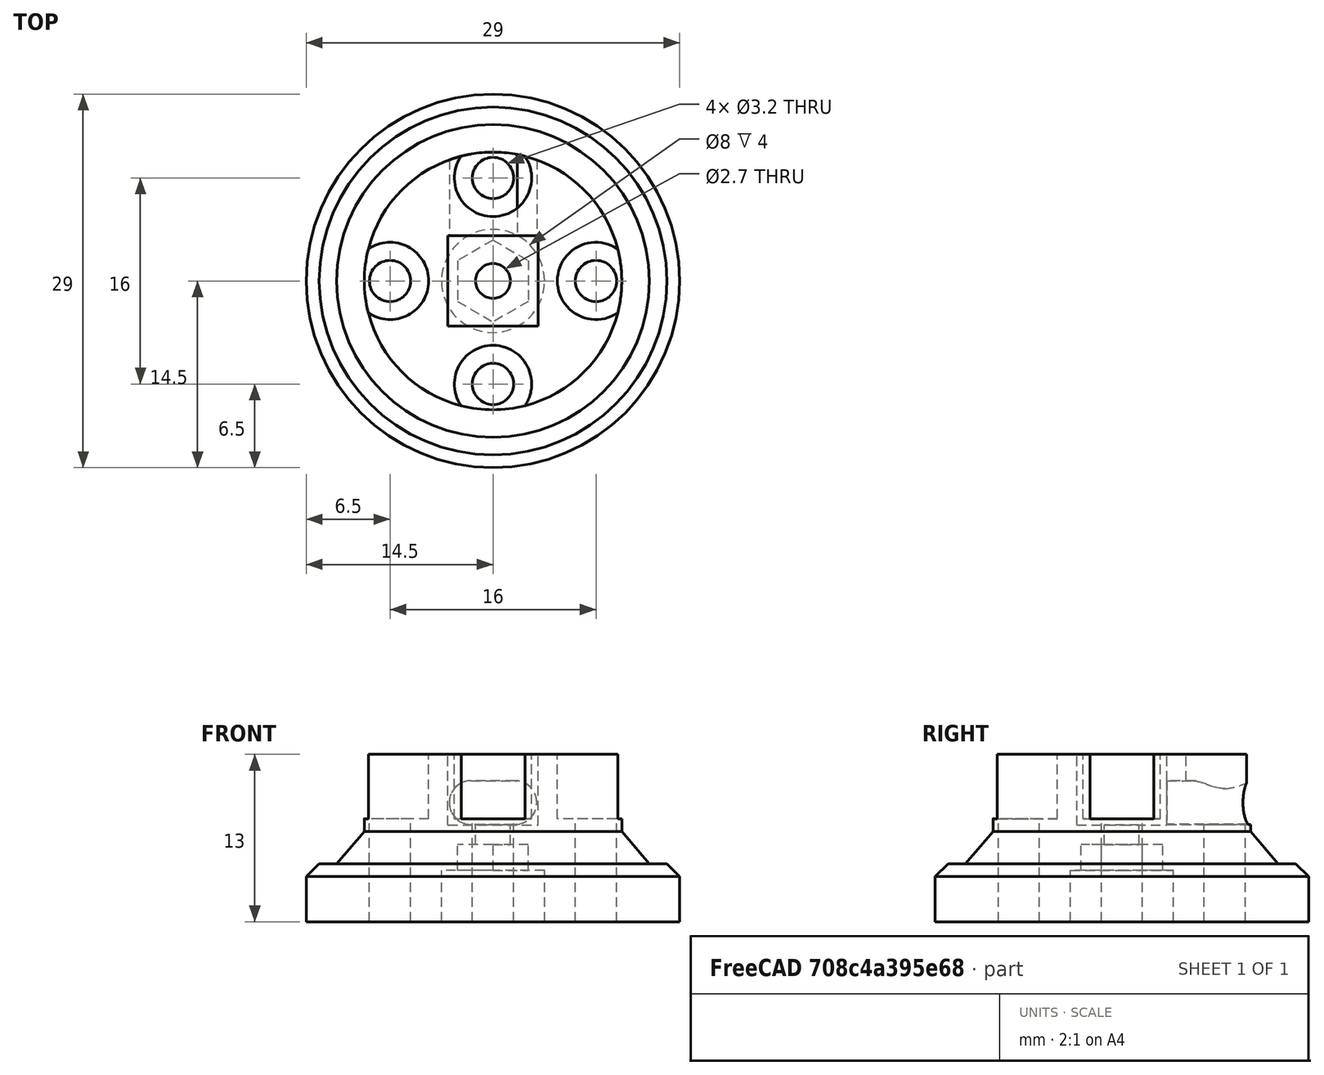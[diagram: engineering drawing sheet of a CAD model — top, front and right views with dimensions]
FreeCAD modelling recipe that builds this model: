
FCSTD DOCUMENT  (FreeCAD 0.15R4671 (Git))
Label: tendon_wheel_ax_fingers
License: CC-BY 3.0
LicenseURL: http://creativecommons.org/licenses/by/3.0/
objects: Part::Cylinder×14, Part::MultiFuse×6, Part::Box×2, Part::Cone×1, Part::Extrusion×1, Part::Mirroring×1, Part::Cut×1, Part::Chamfer×1
note: 27 computed .brp shape members not serialized (recipe doc carries the construction recipe); baked Part::Feature solids carry a one-line shape summary decoded from their .brp

FEATURE [Part::Cylinder] Cylinder
  Angle = 360
  Height = 4.5
  Placement = pos=(0,0,0.5) rot=(0,0,1;0rad)
  Radius = 14.5
FEATURE [Part::Cone] Cone
  Angle = 360
  Height = 3.5
  Placement = pos=(0,0,4) rot=(0,0,1;0rad)
  Radius1 = 13
  Radius2 = 10
FEATURE [Part::Cylinder] Cylinder001
  Angle = 360
  Height = 6.5
  Placement = pos=(0,0,7) rot=(0,0,1;0rad)
  Radius = 10
FEATURE [Part::Cylinder] Cylinder003  label="TopHole003"
  Angle = 360
  Height = 20
  Placement = pos=(-8,0,-7) rot=(0,0,1;0rad)
  Radius = 1.6
FEATURE [Part::Cylinder] Cylinder004  label="TopHole002"
  Angle = 360
  Height = 20
  Placement = pos=(0,-8,-7) rot=(0,0,1;0rad)
  Radius = 1.6
FEATURE [Part::Cylinder] Cylinder005  label="TopHole001"
  Angle = 360
  Height = 20
  Placement = pos=(8,0,-7) rot=(0,0,1;0rad)
  Radius = 1.6
FEATURE [Part::Cylinder] Cylinder006  label="TopHole"
  Angle = 360
  Height = 15
  Placement = pos=(0,8,-7) rot=(0,0,1;0rad)
  Radius = 1.6
FEATURE [Part::Cylinder] Cylinder007  label="TopHole004"
  Angle = 360
  Height = 20
  Placement = pos=(-8,0,3.5) rot=(0,0,1;0rad)
  Radius = 3
FEATURE [Part::Cylinder] Cylinder008  label="TopHole005"
  Angle = 360
  Height = 20
  Placement = pos=(8,0,3.5) rot=(0,0,1;0rad)
  Radius = 3
FEATURE [Part::Cylinder] Cylinder009  label="TopHole006"
  Angle = 360
  Height = 20
  Placement = pos=(0,8,4.5) rot=(0,0,1;0rad)
  Radius = 3
FEATURE [Part::Cylinder] Cylinder010  label="TopHole007"
  Angle = 360
  Height = 20
  Placement = pos=(0,-8,3.5) rot=(0,0,1;0rad)
  Radius = 3
FEATURE [Part::MultiFuse] Fusion001
  Placement = pos=(0,0,5) rot=(0,0,1;0rad)
  Shapes = -> [Cylinder010,Cylinder007,Cylinder005,Cylinder003,Cylinder009,Cylinder004,Cylinder008,Cylinder006]
FEATURE [Part::Cylinder] Cylinder012  label="Cylinder003"
  Angle = 360
  Height = 10
  Placement = pos=(-1.7,12,9.75) rot=(1,0,0;1.5708rad)
  Radius = 1.7
FEATURE [Part::Cylinder] Cylinder013  label="Cylinder004"
  Angle = 360
  Height = 20
  Placement = pos=(0,0,-5) rot=(0,0,1;0rad)
  Radius = 1.35
FEATURE [Part::Box] Box  label="Cube"
  Height = 8
  Length = 7
  Placement = pos=(-3.5,-3.5,8) rot=(0,0,1;0rad)
  Width = 7
FEATURE [Part::Extrusion] Extrude
  Dir = (0,0,2)
  Solid = true
FEATURE [Part::Mirroring] Part__Mirroring  label="Extrude (Mirror #1)"
  Base = (0,0,0)
  Normal = (1,0,0)
  Source = -> Extrude
FEATURE [Part::MultiFuse] Fusion002
  Placement = pos=(0,0,4.5) rot=(0,0,1;0rad)
  Shapes = -> [Part__Mirroring,Extrude]
FEATURE [Part::Cylinder] Cylinder014  label="Cylinder005"
  Angle = 360
  Height = 4.5
  Radius = 4
FEATURE [Part::Cylinder] Cylinder015  label="Cylinder006"
  Angle = 360
  Height = 10
  Placement = pos=(1.7,12,9.75) rot=(1,0,0;1.5708rad)
  Radius = 1.7
FEATURE [Part::Box] Box001  label="Cube001"
  Height = 3.4
  Length = 3.6
  Placement = pos=(-1.7,2,8.05) rot=(0,0,1;0rad)
  Width = 10
FEATURE [Part::MultiFuse] Fusion
  Shapes = -> [Cylinder,Cone,Cylinder001]
FEATURE [Part::MultiFuse] Fusion005
  Shapes = -> [Cylinder014,Fusion002,Cylinder013,Fusion001]
FEATURE [Part::MultiFuse] Fusion006
  Shapes = -> [Cylinder015,Box001,Cylinder012,Box]
FEATURE [Part::MultiFuse] Fusion007
  Shapes = -> [Fusion006,Fusion005]
FEATURE [Part::Cut] Cut
  Base = -> Fusion
  Tool = -> Fusion007
FEATURE [Part::Chamfer] Chamfer
  Base = -> Cut
  Edges = 1 edges r=1: [Edge87]
